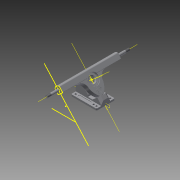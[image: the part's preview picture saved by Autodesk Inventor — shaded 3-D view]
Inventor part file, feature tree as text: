
AUTODESK INVENTOR PART (.ipt)
format: ipt  version: 2015 SP1 (Build 190203100, 203)  size: 442,880 bytes
history: native  units: in
note: dims shown in document units (in); Inventor stores cm internally (conversion verified against a paired STEP export)
features: other x10, sketch x1
ambient origin geometry x8: Origin, YZ Plane, XZ Plane, XY Plane, X Axis, Y Axis, Z Axis, Center Point
bodies: Solid1 (feature_tree)
feature tree (11):
  other  "50cal.iam"
  other  "50cal_baseplate.ipt:1"
  other  "50cal_hanger.ipt:1"
  sketch  "Sketch1"  dims[d0=0.3937in]
  other  "Work Axis1"
  other  "Work Axis2"
  other  "Work Axis3"
  other  "Work Axis1_1"
  other  "Work Axis2_1"
  other  "Work Axis3_1"
  other  "Work Point1"
